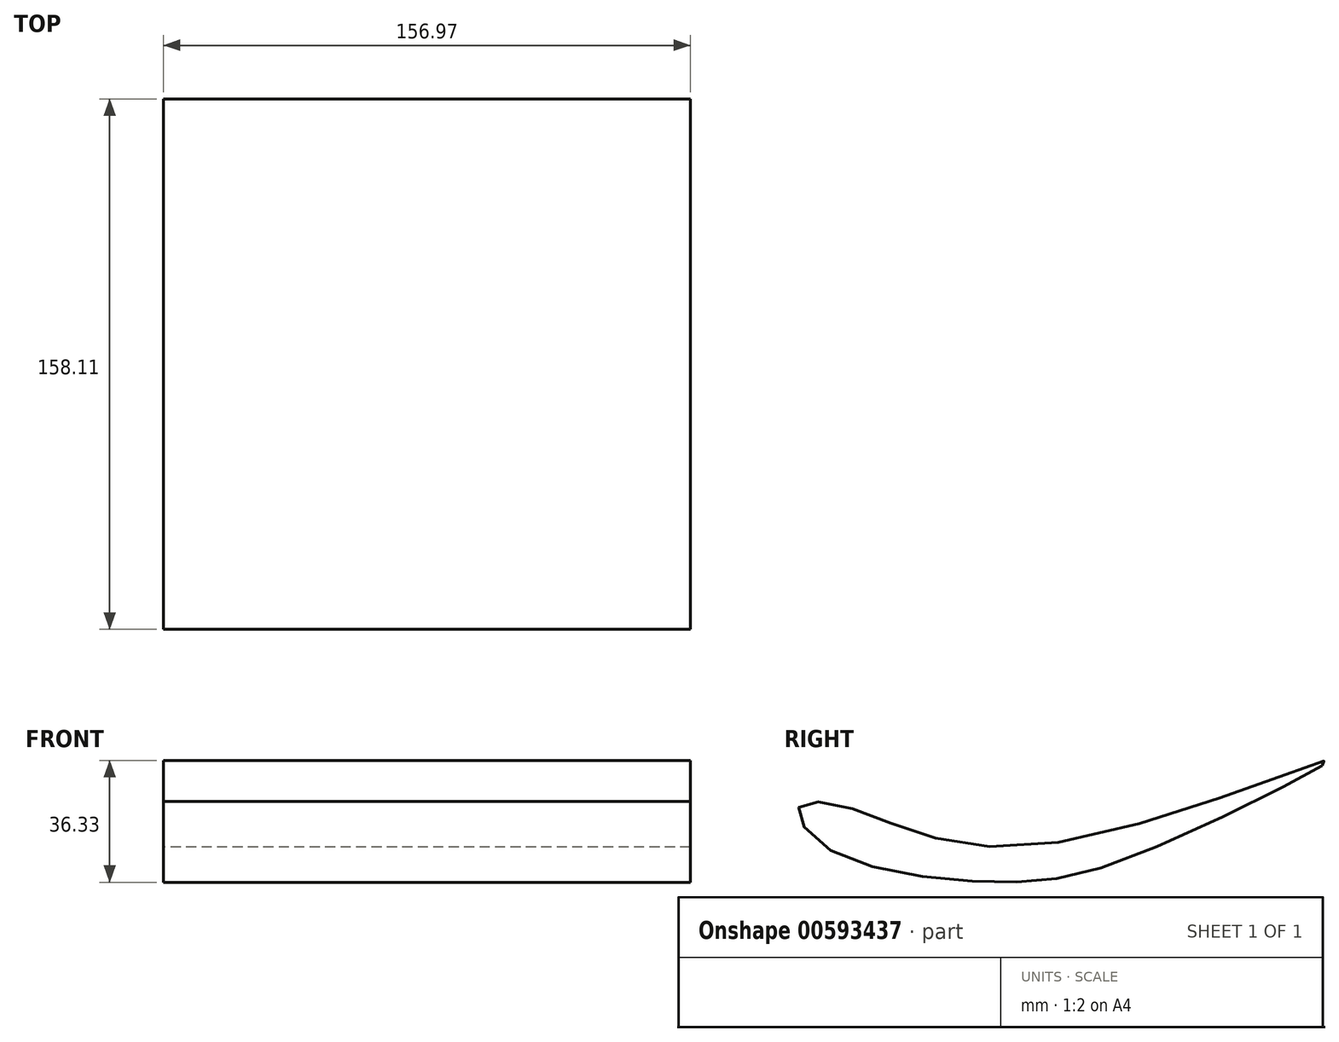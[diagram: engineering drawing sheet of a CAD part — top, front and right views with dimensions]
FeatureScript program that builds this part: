
annotation { "Feature Type Name" : "Feature", "Feature Type Description" : "" }
export const myFeature = defineFeature(function(context is Context, id is Id, definition is map)
    precondition{}
    {
        {
            var Q0;
            Q0=qCreatedBy(makeId("Right.planeOp"),FACE);
            var sketch = newSketch(context, id + "F0", { "sketchPlane" : qUnion([Q0])});
            skFitSpline(sketch, "E0", {"points": [v(-67.1, -3.38) * mm, v(-12.48, -14.24) * mm, v(74.74, 11.01) * mm, v(16.6, -17.47) * mm, v(-26.87, -25.11) * mm, v(-75.04, -14.83) * mm, v(-82.97, -2.8) * mm, v(-67.1, -3.38) * mm]});
            skSolve(sketch);
        }
        {
            var Q0;
            Q0 = qSketchRegion(id + "F0", true);
            extrude(context, id + "F1", {"entities" : qUnion([Q0]), "depth" : 156.97 * mm, "offsetDistance" : 25.4 * mm});
        }
    });
